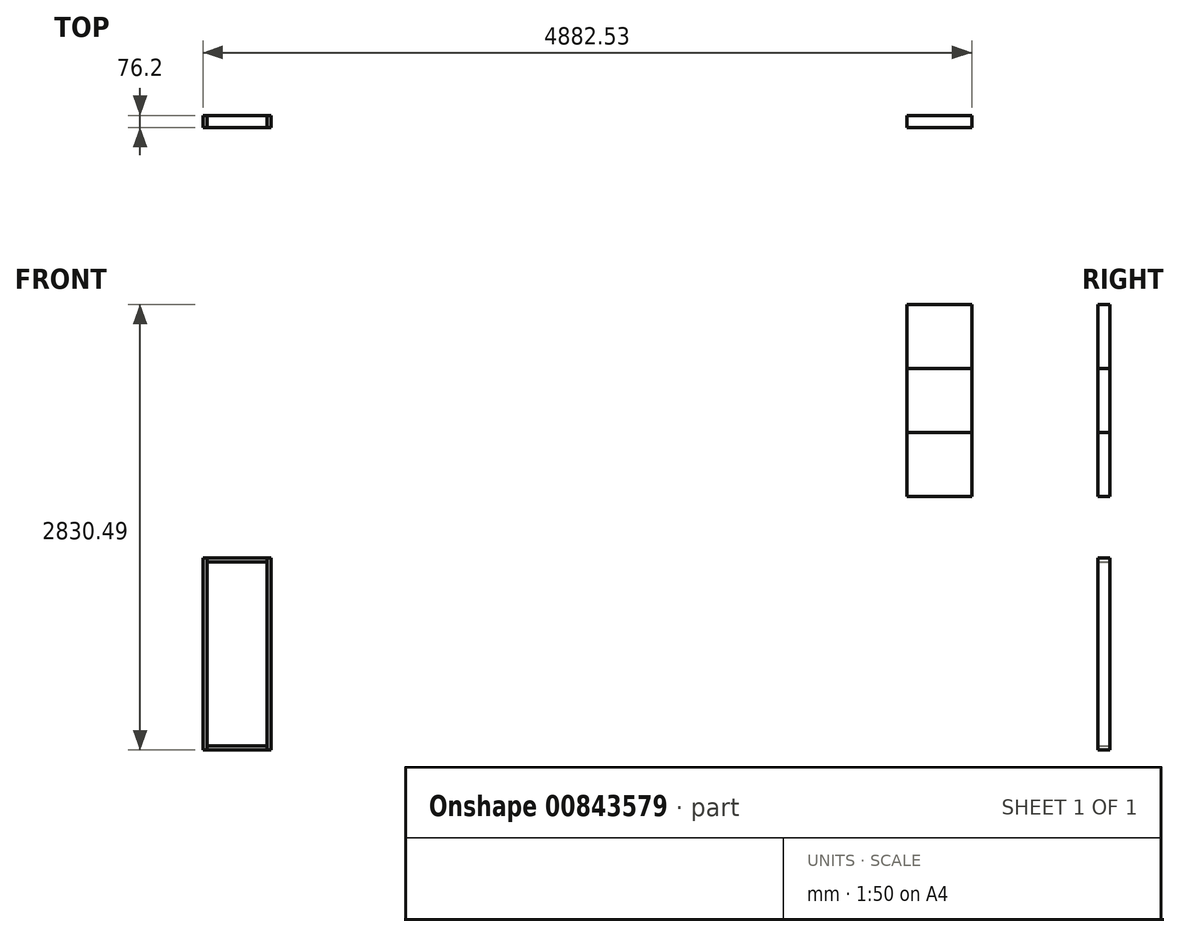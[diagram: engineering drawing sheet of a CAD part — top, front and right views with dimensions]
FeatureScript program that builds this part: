
annotation { "Feature Type Name" : "Feature", "Feature Type Description" : "" }
export const myFeature = defineFeature(function(context is Context, id is Id, definition is map)
    precondition{}
    {
        {
            var Q0;
            Q0=qCreatedBy(makeId("Front.planeOp"),FACE);
            var sketch = newSketch(context, id + "F0", { "sketchPlane" : qUnion([Q0])});
            skLineSegment(sketch, "E0", {"start": v(-431.08, 670.15) * mm, "end": v(-431.08, -549.05) * mm});
            skLineSegment(sketch, "E1", {"start": v(-431.08, 670.15) * mm, "end": v(-456.48, 670.15) * mm});
            skLineSegment(sketch, "E2", {"start": v(-456.48, 670.15) * mm, "end": v(-456.48, -549.05) * mm});
            skLineSegment(sketch, "E3", {"start": v(-431.08, -549.05) * mm, "end": v(-456.48, -549.05) * mm});
            skSolve(sketch);
        }
        {
            var Q0;
            Q0=makeQuery(id+"F0.imprint","IMPRINT",FACE,{"disambiguationData":[TD([[makeQuery(id+"F0.imprint","IMPRINT",EDGE,{"derivedFrom":sQuery(id+"F0.wireOp",EDGE,"E0")}),-1.0]])]});
            extrude(context, id + "F1", {"entities" : qUnion([Q0]), "endBound" : BoundingType.SYMMETRIC, "depth" : 76.2 * mm, "offsetDistance" : 25.4 * mm});
        }
        {
            var Q0;
            Q0=makeQuery(id+"F1.opExtrude","SWEPT_BODY",BODY,{"disambiguationData":[OSD([sQuery(id+"F0.wireOp",EDGE,"E0"),sQuery(id+"F0.wireOp",EDGE,"E1"),sQuery(id+"F0.wireOp",EDGE,"E2"),sQuery(id+"F0.wireOp",EDGE,"E3")])]});
            transform(context, id + "F2", {"entities" : qUnion([Q0]), "transformType" : TransformType.TRANSLATION_3D, "dx" : 652.78 * mm, "dy" : 0 * mm, "dz" : 0 * mm, "makeCopy" : true});
        }
        {
            var Q0;
            Q0=qCreatedBy(makeId("Front.planeOp"),FACE);
            var sketch = newSketch(context, id + "F3", { "sketchPlane" : qUnion([Q0])});
            skLineSegment(sketch, "E4", {"start": v(-381, 828.96) * mm, "end": v(0, 828.96) * mm});
            skLineSegment(sketch, "E5", {"start": v(-381, 828.96) * mm, "end": v(-381, 803.56) * mm});
            skLineSegment(sketch, "E6", {"start": v(-381, 803.56) * mm, "end": v(0, 803.56) * mm});
            skLineSegment(sketch, "E7", {"start": v(0, 828.96) * mm, "end": v(0, 803.56) * mm});
            skSolve(sketch);
        }
        {
            var Q0;
            Q0=makeQuery(id+"F3.imprint","IMPRINT",FACE,{"disambiguationData":[TD([[makeQuery(id+"F3.imprint","IMPRINT",EDGE,{"derivedFrom":sQuery(id+"F3.wireOp",EDGE,"E4")}),-1.0]])]});
            extrude(context, id + "F4", {"entities" : qUnion([Q0]), "endBound" : BoundingType.SYMMETRIC, "depth" : 76.2 * mm, "offsetDistance" : 25.4 * mm});
        }
        {
            var Q0;
            Q0=makeQuery(id+"F4.opExtrude","SWEPT_BODY",BODY,{"disambiguationData":[OSD([sQuery(id+"F3.wireOp",EDGE,"E4"),sQuery(id+"F3.wireOp",EDGE,"E5"),sQuery(id+"F3.wireOp",EDGE,"E6"),sQuery(id+"F3.wireOp",EDGE,"E7")])]});
            transform(context, id + "F5", {"entities" : qUnion([Q0]), "transformType" : TransformType.TRANSLATION_3D, "dx" : 0 * mm, "dy" : 0 * mm, "dz" : -83.82 * mm, "makeCopy" : true});
        }
        {
            var Q0;
            Q0=makeQuery(id+"F5.opPattern","COPY",BODY,{"derivedFrom":makeQuery(id+"F4.opExtrude","SWEPT_BODY",BODY,{"disambiguationData":[OSD([sQuery(id+"F3.wireOp",EDGE,"E4"),sQuery(id+"F3.wireOp",EDGE,"E5"),sQuery(id+"F3.wireOp",EDGE,"E6"),sQuery(id+"F3.wireOp",EDGE,"E7")])]}),"instanceName":"1"});
            transform(context, id + "F6", {"entities" : qUnion([Q0]), "transformType" : TransformType.TRANSLATION_3D, "dx" : 0 * mm, "dy" : 0 * mm, "dz" : -1275.08 * mm, "makeCopy" : false});
        }
        {
            var Q0;
            Q0=makeQuery(id+"F5.opPattern","COPY",BODY,{"derivedFrom":makeQuery(id+"F4.opExtrude","SWEPT_BODY",BODY,{"disambiguationData":[OSD([sQuery(id+"F3.wireOp",EDGE,"E4"),sQuery(id+"F3.wireOp",EDGE,"E5"),sQuery(id+"F3.wireOp",EDGE,"E6"),sQuery(id+"F3.wireOp",EDGE,"E7")])]}),"instanceName":"1"});
            transform(context, id + "F7", {"entities" : qUnion([Q0]), "transformType" : TransformType.TRANSLATION_3D, "dx" : -50.1 * mm, "dy" : 0 * mm, "dz" : 0 * mm, "makeCopy" : false});
        }
        {
            var Q0;
            Q0=makeQuery(id+"F5.opPattern","COPY",BODY,{"derivedFrom":makeQuery(id+"F4.opExtrude","SWEPT_BODY",BODY,{"disambiguationData":[OSD([sQuery(id+"F3.wireOp",EDGE,"E4"),sQuery(id+"F3.wireOp",EDGE,"E5"),sQuery(id+"F3.wireOp",EDGE,"E6"),sQuery(id+"F3.wireOp",EDGE,"E7")])]}),"instanceName":"1"});
            transform(context, id + "F8", {"entities" : qUnion([Q0]), "transformType" : TransformType.TRANSLATION_3D, "dx" : 0 * mm, "dy" : 0 * mm, "dz" : 6.3 * mm, "makeCopy" : false});
        }
        {
            var Q0;
            Q0=makeQuery(id+"F4.opExtrude","SWEPT_BODY",BODY,{"disambiguationData":[OSD([sQuery(id+"F3.wireOp",EDGE,"E4"),sQuery(id+"F3.wireOp",EDGE,"E5"),sQuery(id+"F3.wireOp",EDGE,"E6"),sQuery(id+"F3.wireOp",EDGE,"E7")])]});
            transform(context, id + "F9", {"entities" : qUnion([Q0]), "transformType" : TransformType.TRANSLATION_3D, "dx" : -40.64 * mm, "dy" : 0 * mm, "dz" : -156.72 * mm, "makeCopy" : false});
        }
        {
            var Q0;
            Q0=makeQuery(id+"F4.opExtrude","SWEPT_BODY",BODY,{"disambiguationData":[OSD([sQuery(id+"F3.wireOp",EDGE,"E4"),sQuery(id+"F3.wireOp",EDGE,"E5"),sQuery(id+"F3.wireOp",EDGE,"E6"),sQuery(id+"F3.wireOp",EDGE,"E7")])]});
            transform(context, id + "F10", {"entities" : qUnion([Q0]), "transformType" : TransformType.TRANSLATION_3D, "dx" : -9.45 * mm, "dy" : 0 * mm, "dz" : -2.08 * mm, "makeCopy" : false});
        }
        {
            var Q0;
            Q0=makeQuery(id+"F2.opPattern","COPY",BODY,{"derivedFrom":makeQuery(id+"F1.opExtrude","SWEPT_BODY",BODY,{"disambiguationData":[OSD([sQuery(id+"F0.wireOp",EDGE,"E0"),sQuery(id+"F0.wireOp",EDGE,"E1"),sQuery(id+"F0.wireOp",EDGE,"E2"),sQuery(id+"F0.wireOp",EDGE,"E3")])]}),"instanceName":"1"});
            transform(context, id + "F11", {"entities" : qUnion([Q0]), "transformType" : TransformType.TRANSLATION_3D, "dx" : -226.06 * mm, "dy" : 0 * mm, "dz" : 0 * mm, "makeCopy" : false});
        }
        {
            var Q0;
            Q0=makeQuery(id+"F2.opPattern","COPY",BODY,{"derivedFrom":makeQuery(id+"F1.opExtrude","SWEPT_BODY",BODY,{"disambiguationData":[OSD([sQuery(id+"F0.wireOp",EDGE,"E0"),sQuery(id+"F0.wireOp",EDGE,"E1"),sQuery(id+"F0.wireOp",EDGE,"E2"),sQuery(id+"F0.wireOp",EDGE,"E3")])]}),"instanceName":"1"});
            transform(context, id + "F12", {"entities" : qUnion([Q0]), "transformType" : TransformType.TRANSLATION_3D, "dx" : -20.32 * mm, "dy" : 0 * mm, "dz" : 0 * mm, "makeCopy" : false});
        }
        {
            var Q0;
            Q0=makeQuery(id+"F2.opPattern","COPY",BODY,{"derivedFrom":makeQuery(id+"F1.opExtrude","SWEPT_BODY",BODY,{"disambiguationData":[OSD([sQuery(id+"F0.wireOp",EDGE,"E0"),sQuery(id+"F0.wireOp",EDGE,"E1"),sQuery(id+"F0.wireOp",EDGE,"E2"),sQuery(id+"F0.wireOp",EDGE,"E3")])]}),"instanceName":"1"});
            transform(context, id + "F13", {"entities" : qUnion([Q0]), "transformType" : TransformType.TRANSLATION_3D, "dx" : 0 * mm, "dy" : 0 * mm, "dz" : 0 * mm, "makeCopy" : false});
        }
        {
            var Q0;
            Q0=makeQuery(id+"F2.opPattern","COPY",BODY,{"derivedFrom":makeQuery(id+"F1.opExtrude","SWEPT_BODY",BODY,{"disambiguationData":[OSD([sQuery(id+"F0.wireOp",EDGE,"E0"),sQuery(id+"F0.wireOp",EDGE,"E1"),sQuery(id+"F0.wireOp",EDGE,"E2"),sQuery(id+"F0.wireOp",EDGE,"E3")])]}),"instanceName":"1"});
            transform(context, id + "F14", {"entities" : qUnion([Q0]), "transformType" : TransformType.TRANSLATION_3D, "dx" : 0 * mm, "dy" : 0 * mm, "dz" : 0 * mm, "makeCopy" : false});
        }
        {
            var Q0;
            Q0=qCreatedBy(makeId("Front.planeOp"),FACE);
            var sketch = newSketch(context, id + "F15", { "sketchPlane" : qUnion([Q0])});
            skLineSegment(sketch, "E8.bottom", {"start": v(4013.3, 2281.44) * mm, "end": v(4426.05, 2281.44) * mm});
            skLineSegment(sketch, "E8.top", {"start": v(4013.3, 1875.04) * mm, "end": v(4426.05, 1875.04) * mm});
            skLineSegment(sketch, "E8.left", {"start": v(4013.3, 2281.44) * mm, "end": v(4013.3, 1875.04) * mm});
            skLineSegment(sketch, "E8.right", {"start": v(4426.05, 2281.44) * mm, "end": v(4426.05, 1875.04) * mm});
            skSolve(sketch);
        }
        {
            var Q0;
            Q0=makeQuery(id+"F15.imprint","IMPRINT",FACE,{"disambiguationData":[TD([[makeQuery(id+"F15.imprint","IMPRINT",EDGE,{"derivedFrom":sQuery(id+"F15.wireOp",EDGE,"E8.bottom")}),-1.0]])]});
            extrude(context, id + "F16", {"entities" : qUnion([Q0]), "endBound" : BoundingType.SYMMETRIC, "depth" : 76.2 * mm, "offsetDistance" : 25.4 * mm});
        }
        {
            var Q0;
            Q0=makeQuery(id+"F16.opExtrude","SWEPT_BODY",BODY,{"disambiguationData":[OSD([sQuery(id+"F15.wireOp",EDGE,"E8.bottom"),sQuery(id+"F15.wireOp",EDGE,"E8.top"),sQuery(id+"F15.wireOp",EDGE,"E8.left"),sQuery(id+"F15.wireOp",EDGE,"E8.right")])]});
            transform(context, id + "F17", {"entities" : qUnion([Q0]), "transformType" : TransformType.TRANSLATION_3D, "dx" : 0 * mm, "dy" : 0 * mm, "dz" : -459.74 * mm, "makeCopy" : true});
        }
        {
            var Q0;
            Q0=makeQuery(id+"F17.opPattern","COPY",BODY,{"derivedFrom":makeQuery(id+"F16.opExtrude","SWEPT_BODY",BODY,{"disambiguationData":[OSD([sQuery(id+"F15.wireOp",EDGE,"E8.bottom"),sQuery(id+"F15.wireOp",EDGE,"E8.top"),sQuery(id+"F15.wireOp",EDGE,"E8.left"),sQuery(id+"F15.wireOp",EDGE,"E8.right")])]}),"instanceName":"1"});
            transform(context, id + "F18", {"entities" : qUnion([Q0]), "transformType" : TransformType.TRANSLATION_3D, "dx" : 0 * mm, "dy" : 0 * mm, "dz" : -492.76 * mm, "makeCopy" : true});
        }
        {
            var Q0;
            Q0=makeQuery(id+"F17.opPattern","COPY",BODY,{"derivedFrom":makeQuery(id+"F16.opExtrude","SWEPT_BODY",BODY,{"disambiguationData":[OSD([sQuery(id+"F15.wireOp",EDGE,"E8.bottom"),sQuery(id+"F15.wireOp",EDGE,"E8.top"),sQuery(id+"F15.wireOp",EDGE,"E8.left"),sQuery(id+"F15.wireOp",EDGE,"E8.right")])]}),"instanceName":"1"});
            transform(context, id + "F19", {"entities" : qUnion([Q0]), "transformType" : TransformType.TRANSLATION_3D, "dx" : 0 * mm, "dy" : 0 * mm, "dz" : 53.34 * mm, "makeCopy" : false});
        }
        {
            var Q0;
            Q0=makeQuery(id+"F18.opPattern","COPY",BODY,{"derivedFrom":makeQuery(id+"F17.opPattern","COPY",BODY,{"derivedFrom":makeQuery(id+"F16.opExtrude","SWEPT_BODY",BODY,{"disambiguationData":[OSD([sQuery(id+"F15.wireOp",EDGE,"E8.bottom"),sQuery(id+"F15.wireOp",EDGE,"E8.top"),sQuery(id+"F15.wireOp",EDGE,"E8.left"),sQuery(id+"F15.wireOp",EDGE,"E8.right")])]}),"instanceName":"1"}),"instanceName":"1"});
            transform(context, id + "F20", {"entities" : qUnion([Q0]), "transformType" : TransformType.TRANSLATION_3D, "dx" : 0 * mm, "dy" : 0 * mm, "dz" : 139.7 * mm, "makeCopy" : false});
        }
    });
